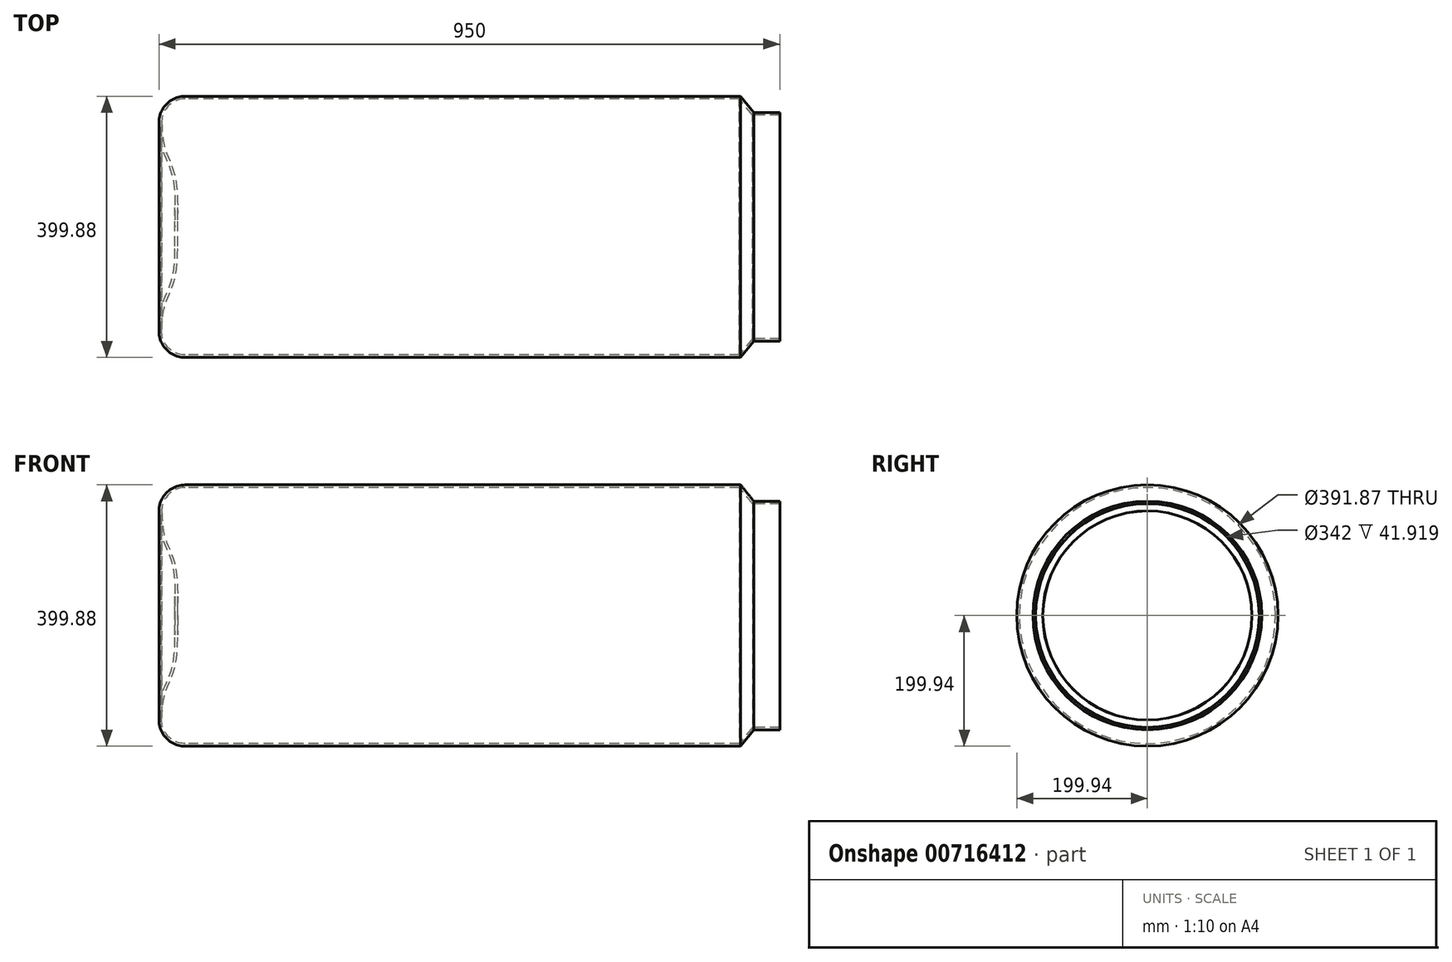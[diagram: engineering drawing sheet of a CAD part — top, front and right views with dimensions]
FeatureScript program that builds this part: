
annotation { "Feature Type Name" : "Feature", "Feature Type Description" : "" }
export const myFeature = defineFeature(function(context is Context, id is Id, definition is map)
    precondition{}
    {
        {
            var Q0;
            Q0=qCreatedBy(makeId("Top.planeOp"),FACE);
            var sketch = newSketch(context, id + "F0", { "sketchPlane" : qUnion([Q0])});
            skLineSegment(sketch, "E0", {"start": v(-590.45, 0) * mm, "end": v(0, 0) * mm, "construction": true});
            skLineSegment(sketch, "E1.bottom", {"start": v(0, 0) * mm, "end": v(950, 0) * mm});
            skLineSegment(sketch, "E1.top", {"start": v(40, 199.94) * mm, "end": v(890, 199.94) * mm});
            skPoint(sketch, "E2.visualSharp", {"position": v(-5.02, 199.94) * mm});
            skArc(sketch, "E2.filletArc", {"start": v(40, 199.94) * mm, "mid": v(11.74, 188.24) * mm, "end": v(0, 160) * mm});
            skPoint(sketch, "E3.visualSharp", {"position": v(0, 0) * mm});
            skPoint(sketch, "E4.2.internal.snap0", {"position": v(0, 80) * mm});
            skLineSegment(sketch, "E5", {"start": v(950, 0) * mm, "end": v(950, 175) * mm});
            skFitSpline(sketch, "E6", {"points": [v(0, 160) * mm, v(5.13, 119.2) * mm, v(17.77, 86.75) * mm, v(24.04, 49.27) * mm, v(24, 0) * mm], "startDerivative": vector(9.28, -168.98) * mm, "endDerivative": vector(-4.7, -184.25) * mm});
            skLineSegment(sketch, "E7.trimOffspring", {"start": v(24, 0) * mm, "end": v(619.1, 0) * mm, "construction": true});
            skLineSegment(sketch, "E8", {"start": v(950, 175) * mm, "end": v(910, 175) * mm});
            skLineSegment(sketch, "E9", {"start": v(910, 175) * mm, "end": v(890, 199.94) * mm});
            skSolve(sketch);
        }
        {
            var Q0;
            Q0 = qSketchRegion(id + "F0", true);
            var Q1;
            Q1=sQuery(id+"F0.wireOp",EDGE,"E0");
            revolve(context, id + "F1", {"surfaceOperationType" : NewSurfaceOperationType.NEW, "entities" : qUnion([Q0]), "axis" : qUnion([Q1]), "revolveType" : RevolveType.FULL});
        }
        {
            var Q0;
            Q0=makeQuery(id+"F1.opRevolve","SWEPT_FACE",FACE,{"disambiguationData":[OSD([sQuery(id+"F0.wireOp",EDGE,"E5")])]});
            shell(context, id + "F2", {"entities" : qUnion([Q0]), "thickness" : 4 * mm});
        }
    });
